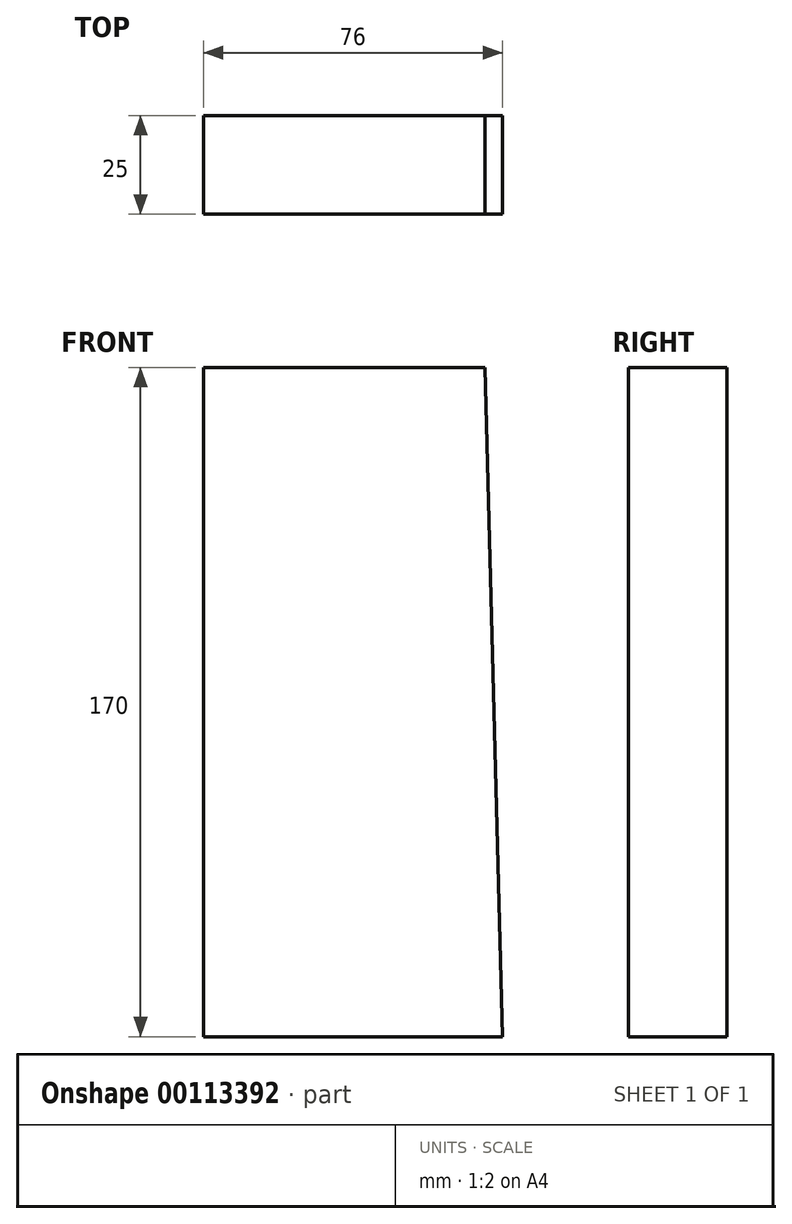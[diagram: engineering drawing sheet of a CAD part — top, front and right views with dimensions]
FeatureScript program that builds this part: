
annotation { "Feature Type Name" : "Feature", "Feature Type Description" : "" }
export const myFeature = defineFeature(function(context is Context, id is Id, definition is map)
    precondition{}
    {
        {
            var Q0;
            Q0=qCreatedBy(makeId("Front.planeOp"),FACE);
            var sketch = newSketch(context, id + "F0", { "sketchPlane" : qUnion([Q0])});
            skLineSegment(sketch, "E0", {"start": v(0, 0) * mm, "end": v(0, 170) * mm});
            skLineSegment(sketch, "E1", {"start": v(0, 170) * mm, "end": v(71.5, 170) * mm});
            skLineSegment(sketch, "E2", {"start": v(0, 0) * mm, "end": v(76, 0) * mm});
            skLineSegment(sketch, "E3", {"start": v(71.5, 170) * mm, "end": v(76, 0) * mm});
            skSolve(sketch);
        }
        {
            var Q0;
            Q0=makeQuery(id+"F0.imprint","IMPRINT",FACE,{"disambiguationData":[TD([[makeQuery(id+"F0.imprint","IMPRINT",EDGE,{"derivedFrom":sQuery(id+"F0.wireOp",EDGE,"E0")}),-1.0]])]});
            extrude(context, id + "F1", {"entities" : qUnion([Q0]), "depth" : 25 * mm});
        }
    });
